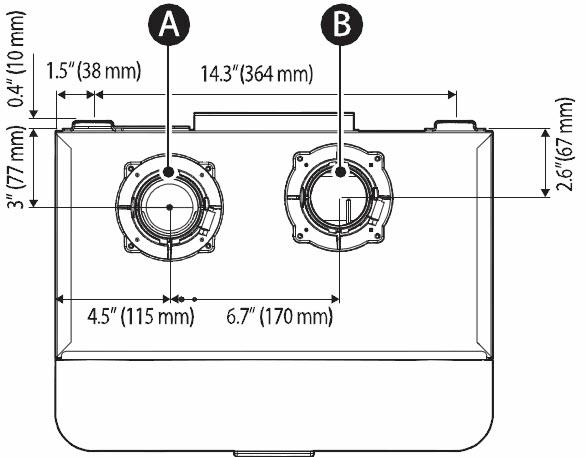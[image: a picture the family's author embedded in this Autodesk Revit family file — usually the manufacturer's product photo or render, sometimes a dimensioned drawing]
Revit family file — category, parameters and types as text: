
# Revit family: Water_Heater-Racks-Navien-NPE-2_Unit_Front-02
name_source: partatom
category: Mechanical Equipment
revit_build: Autodesk Revit 2016 (Build: 20150220_1215(x64)
units: mm (PartAtom-declared; Revit-internal decimal feet)

## family parameters
Cut with Voids When Loaded = No
Host = Face
OmniClass Number = 23.65.35.11
OmniClass Title = Supply Water Heaters
Part Type = Normal
Room Calculation Point = No
Round Connector Dimension = Use Diameter
Shared = No

## types (4) — shared parameters
2" Exhaust/Intake = Yes
3" Exhaust/Intake = No
Apparent Load = 0 VA
Assembly Code = D3010500
Certifications = Energy Star | AHRI | CSA | CSA | NFS
Cold Water Inlet = 1"
Configuration = NPE_F2_2F
Default Elevation = 48 "
Depth = 23.8 "
Description = 2 Unit Front
Exhaust = 2"
Finish = Metal - Navien - White
Flow Rate = 1 GPM
Flow Rate Note = 35°F (19°C) temp rise: 11.2 GPM (42 L/m) | 45°F (25°C) temp rise: 8.7 GPM (33 L/m) | 67°F (36°C) temp rise: NPE-240A: 5.6 GPM(21 L/m), NPE-240S: 5.7 GPM(22 L/m)
Frequency = 60 Hz
Gas Inlet = 1"
Heating Capacity = 120000.0 Btu/h
Heating Capacity Note = 19,900–199,900 (BTU/H)
Height = 65.5 "
Hot Water Outlet = 1"
Ignition = Electronic ignition
Installation Type = Indoor
Intake = 2"
Keynote = 22 33 00.A1
Manifold(s) = (1) 30019040A
Manufacturer = Navien, Inc.
Manufacturer Fax Number = (949) 420-0430
Natural Gas Manifold Pressure = -0.05" WC to -0.58" WC
Natural Gas Supply Pressure = 3.5"–10.5" WC
Number of Poles = 1
Phase = 1
Power Factor = 1
Product Documentation Link = https://www.navieninc.com
Product Name = NPE Series Tankless Water Heaters w/ Racks
Product Page URL = https://www.navieninc.com
Propane Gas Manifold Pressure = -0.10" WC to -0.78" WC
Propane Gas Supply Pressure = 8"–13" WC
Rack(s) = (1) GFFM-KDIZUS-003 + (1) GFFM-KDIZUS-004
Required Cascade Operation Accessory = (2) 30014367A (Common Vent Damper & Cascade Communication Cable) or (1) GXXX000546 (Individual Vent Cascade Communication Cable)
Type Comments = For Wall Mount RL Manifold systems- Exclude Base & Add-on Racks
URL = https://www.navieninc.com
Venting = Exhaust: 2" PVC, CPVC, PP, SS / 2" special gas vent type BH (Class II, A/B/C) | Intake: 2" PVC, CPVC, PP, SS / 2" special gas vent type BH (Class II, A/B/C) | Vent clearances: 0" to combustibles
Venting Type = Forced draft direct vent
Version = 2016 - v1.0.a
Voltage = 120 V
Water Pressure = 15–150 PSI
Wi-Fi Ready = NaviLink Wi-Fi Control: PBCM-AS-001
Width = 42.3 "

## per-type parameters (varying)
| type | Constraints | Model | Natural Gas | Propane Gas | Recirculation Inlet | Recirculation Inlet Visibility | Tankless Water Heaters | Weight |
| Natural Gas - Recirculating System - NPE-240A(Advanced)-NG | 6 | (2) NPE-240A-NG | Yes | No | 0" | Yes | (2) NPE-240A-NG | 82.00 lbf |
| Natural Gas - NPE-240S(Standard)-NG | 7 | (2) NPE-240S-NG | Yes | No | 1" | No | (2) NPE-240S-NG | 75.00 lbf |
| Propane Gas - Recirculating System - NPE-240A(Advanced)-LPG | 6 | (2) NPE-240A-LPG | No | Yes | 0" | Yes | (2) NPE-240A-LPG | 82.00 lbf |
| Propane Gas - NPE-240S(Standard)-LPG | 7 | (2) NPE-240S-LPG | No | Yes | 1" | No | (2) NPE-240S-LPG | 75.00 lbf |

## geometry (parser evidence)
native form markers: Sweep x16
no freeform markers — native parametric forms only
